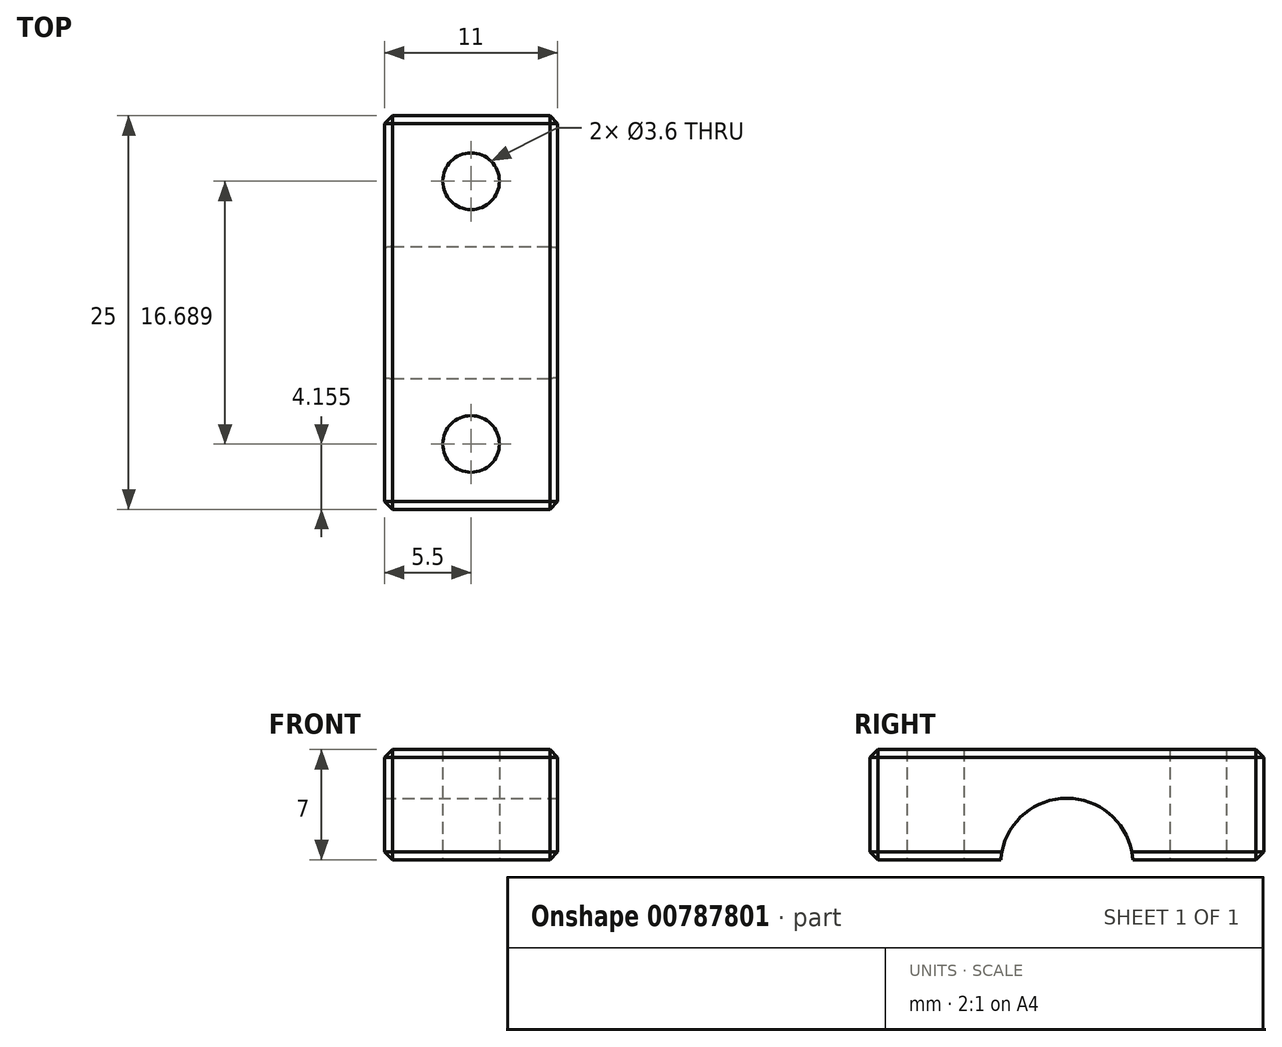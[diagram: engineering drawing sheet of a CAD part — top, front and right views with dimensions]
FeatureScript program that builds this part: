
annotation { "Feature Type Name" : "Feature", "Feature Type Description" : "" }
export const myFeature = defineFeature(function(context is Context, id is Id, definition is map)
    precondition{}
    {
        {
            var Q0;
            Q0=qCreatedBy(makeId("Top.planeOp"),FACE);
            var sketch = newSketch(context, id + "F0", { "sketchPlane" : qUnion([Q0])});
            skLineSegment(sketch, "E0.bottom", {"start": v(5.5, 12.5) * mm, "end": v(-5.5, 12.5) * mm});
            skLineSegment(sketch, "E0.top", {"start": v(5.5, -12.5) * mm, "end": v(-5.5, -12.5) * mm});
            skLineSegment(sketch, "E0.left", {"start": v(5.5, 12.5) * mm, "end": v(5.5, -12.5) * mm});
            skLineSegment(sketch, "E0.right", {"start": v(-5.5, 12.5) * mm, "end": v(-5.5, -12.5) * mm});
            skPoint(sketch, "E0.middle", {"position": v(0, 0) * mm});
            skSolve(sketch);
        }
        {
            var Q0;
            Q0=makeQuery(id+"F0.imprint","IMPRINT",FACE,{"disambiguationData":[TD([[makeQuery(id+"F0.imprint","IMPRINT",EDGE,{"derivedFrom":sQuery(id+"F0.wireOp",EDGE,"E0.bottom")}),1.0]])]});
            extrude(context, id + "F1", {"entities" : qUnion([Q0]), "depth" : 7 * mm, "offsetDistance" : 25 * mm});
        }
        {
            var Q0;
            Q0=makeQuery(id+"F1.opExtrude","SWEPT_FACE",FACE,{"disambiguationData":[OSD([sQuery(id+"F0.wireOp",EDGE,"E0.left")])]});
            var sketch = newSketch(context, id + "F2", { "sketchPlane" : qUnion([Q0])});
            skCircle(sketch, "E1", {"center": v(0, -0.3) * mm, "radius": 4.2 * mm});
            skSolve(sketch);
        }
        {
            var Q0;
            {var subQ0=sQuery(id+"F2.wireOp",EDGE,"E1");var subQ1=makeQuery(id+"F1.opExtrude","CAP_EDGE",EDGE,{"disambiguationData":[OSD([sQuery(id+"F0.wireOp",EDGE,"E0.left")])],"isStart":true});var subQ2=makeQuery(id+"F2.imprint","INTERSECT",VERTEX,{"disambiguationData":[OD(0.0)],"derivedFrom":[subQ1,subQ0]});Q0=makeQuery(id+"F2.imprint","IMPRINT",FACE,{"disambiguationData":[TD([[makeQuery(id+"F2.imprint","IMPRINT",EDGE,{"disambiguationData":[TD([[subQ2,-1.0]])],"derivedFrom":subQ0}),1.0]])]});}
            extrude(context, id + "F3", {"entities" : qUnion([Q0]), "operationType" : NewBodyOperationType.REMOVE, "endBound" : BoundingType.UP_TO_NEXT, "oppositeDirection" : true, "depth" : 25 * mm, "offsetDistance" : 25 * mm});
        }
        {
            var Q0;
            {var subQ0=sQuery(id+"F0.wireOp",EDGE,"E0.bottom");var subQ1=sQuery(id+"F0.wireOp",EDGE,"E0.right");var subQ2=sQuery(id+"F0.wireOp",EDGE,"E0.left");Q0=makeQuery(id+"F3.boolean.opBoolean","SPLIT",FACE,{"disambiguationData":[TD([makeQuery(id+"F1.opExtrude","SWEPT_FACE",FACE,{"disambiguationData":[OSD([subQ0])]})])],"derivedFrom":makeQuery(id+"F1.opExtrude","CAP_FACE",FACE,{"disambiguationData":[OSD([subQ0,sQuery(id+"F0.wireOp",EDGE,"E0.top"),subQ2,subQ1])],"isStart":true})});}
            var sketch = newSketch(context, id + "F4", { "sketchPlane" : qUnion([Q0])});
            skCircle(sketch, "E2", {"center": v(0, -8.34) * mm, "radius": 1.8 * mm});
            skPoint(sketch, "E2.centerSnap0", {"position": v(-5.5, -8.34) * mm});
            skLineSegment(sketch, "E3.0", {"start": v(-5.5, 4.19) * mm, "end": v(-5.5, 12.5) * mm});
            skCircle(sketch, "E4", {"center": v(0, 8.34) * mm, "radius": 1.8 * mm});
            skPoint(sketch, "E4.centerSnap0", {"position": v(-5.5, 8.34) * mm});
            skSolve(sketch);
        }
        {
            var Q0;
            Q0=makeQuery(id+"F4.imprint","IMPRINT",FACE,{"disambiguationData":[TD([[makeQuery(id+"F4.imprint","IMPRINT",EDGE,{"derivedFrom":sQuery(id+"F4.wireOp",EDGE,"E4")}),1.0]])]});
            var Q1;
            Q1=makeQuery(id+"F4.imprint","IMPRINT",FACE,{"disambiguationData":[TD([[makeQuery(id+"F4.imprint","IMPRINT",EDGE,{"derivedFrom":sQuery(id+"F4.wireOp",EDGE,"E2")}),1.0]])]});
            extrude(context, id + "F5", {"entities" : qUnion([Q0, Q1]), "operationType" : NewBodyOperationType.REMOVE, "endBound" : BoundingType.UP_TO_NEXT, "oppositeDirection" : true, "depth" : 25 * mm, "offsetDistance" : 25 * mm});
        }
        {
            var Q0;
            Q0=makeQuery(id+"F3.boolean.opBoolean","COPY",EDGE,{"derivedFrom":makeQuery(id+"F3.opExtrude","CAP_EDGE",EDGE,{"disambiguationData":[OSD([sQuery(id+"F2.wireOp",EDGE,"E1")])],"isStart":true})});
            var Q1;
            {var subQ0=sQuery(id+"F0.wireOp",EDGE,"E0.bottom");var subQ1=sQuery(id+"F0.wireOp",EDGE,"E0.left");Q1=makeQuery(id+"F3.boolean.opBoolean","SPLIT",EDGE,{"disambiguationData":[TD([makeQuery(id+"F1.opExtrude","SWEPT_FACE",FACE,{"disambiguationData":[OSD([subQ0])]})])],"derivedFrom":makeQuery(id+"F1.opExtrude","CAP_EDGE",EDGE,{"disambiguationData":[OSD([subQ1])],"isStart":true})});}
            var Q2;
            Q2=makeQuery(id+"F1.opExtrude","CAP_EDGE",EDGE,{"disambiguationData":[OSD([sQuery(id+"F0.wireOp",EDGE,"E0.bottom")])],"isStart":true});
            var Q3;
            {var subQ0=sQuery(id+"F0.wireOp",EDGE,"E0.bottom");var subQ1=sQuery(id+"F0.wireOp",EDGE,"E0.right");Q3=makeQuery(id+"F3.boolean.opBoolean","SPLIT",EDGE,{"disambiguationData":[TD([makeQuery(id+"F1.opExtrude","SWEPT_FACE",FACE,{"disambiguationData":[OSD([subQ0])]})])],"derivedFrom":makeQuery(id+"F1.opExtrude","CAP_EDGE",EDGE,{"disambiguationData":[OSD([subQ1])],"isStart":true})});}
            var Q4;
            {var subQ0=sQuery(id+"F0.wireOp",EDGE,"E0.left");var subQ1=sQuery(id+"F0.wireOp",EDGE,"E0.top");Q4=makeQuery(id+"F3.boolean.opBoolean","SPLIT",EDGE,{"disambiguationData":[TD([makeQuery(id+"F1.opExtrude","SWEPT_FACE",FACE,{"disambiguationData":[OSD([subQ1])]})])],"derivedFrom":makeQuery(id+"F1.opExtrude","CAP_EDGE",EDGE,{"disambiguationData":[OSD([subQ0])],"isStart":true})});}
            var Q5;
            Q5=makeQuery(id+"F1.opExtrude","CAP_EDGE",EDGE,{"disambiguationData":[OSD([sQuery(id+"F0.wireOp",EDGE,"E0.top")])],"isStart":true});
            var Q6;
            {var subQ0=sQuery(id+"F0.wireOp",EDGE,"E0.right");var subQ1=sQuery(id+"F0.wireOp",EDGE,"E0.top");Q6=makeQuery(id+"F3.boolean.opBoolean","SPLIT",EDGE,{"disambiguationData":[TD([makeQuery(id+"F1.opExtrude","SWEPT_FACE",FACE,{"disambiguationData":[OSD([subQ1])]})])],"derivedFrom":makeQuery(id+"F1.opExtrude","CAP_EDGE",EDGE,{"disambiguationData":[OSD([subQ0])],"isStart":true})});}
            var Q7;
            Q7=makeQuery(id+"F1.opExtrude","SWEPT_EDGE",EDGE,{"disambiguationData":[OSD([sQuery(id+"F0.wireOp",EDGE,"E0.top"),sQuery(id+"F0.wireOp",EDGE,"E0.left")])]});
            var Q8;
            Q8=makeQuery(id+"F1.opExtrude","CAP_EDGE",EDGE,{"disambiguationData":[OSD([sQuery(id+"F0.wireOp",EDGE,"E0.top")])],"isStart":false});
            var Q9;
            Q9=makeQuery(id+"F1.opExtrude","SWEPT_EDGE",EDGE,{"disambiguationData":[OSD([sQuery(id+"F0.wireOp",EDGE,"E0.top"),sQuery(id+"F0.wireOp",EDGE,"E0.right")])]});
            var Q10;
            Q10=makeQuery(id+"F1.opExtrude","CAP_EDGE",EDGE,{"disambiguationData":[OSD([sQuery(id+"F0.wireOp",EDGE,"E0.left")])],"isStart":false});
            var Q11;
            Q11=makeQuery(id+"F1.opExtrude","SWEPT_EDGE",EDGE,{"disambiguationData":[OSD([sQuery(id+"F0.wireOp",EDGE,"E0.bottom"),sQuery(id+"F0.wireOp",EDGE,"E0.left")])]});
            var Q12;
            Q12=makeQuery(id+"F1.opExtrude","CAP_EDGE",EDGE,{"disambiguationData":[OSD([sQuery(id+"F0.wireOp",EDGE,"E0.bottom")])],"isStart":false});
            var Q13;
            Q13=makeQuery(id+"F1.opExtrude","SWEPT_EDGE",EDGE,{"disambiguationData":[OSD([sQuery(id+"F0.wireOp",EDGE,"E0.bottom"),sQuery(id+"F0.wireOp",EDGE,"E0.right")])]});
            var Q14;
            Q14=makeQuery(id+"F1.opExtrude","CAP_EDGE",EDGE,{"disambiguationData":[OSD([sQuery(id+"F0.wireOp",EDGE,"E0.right")])],"isStart":false});
            var Q15;
            {var subQ0=sQuery(id+"F2.wireOp",EDGE,"E1");var subQ1=makeQuery(id+"F1.opExtrude","CAP_EDGE",EDGE,{"disambiguationData":[OSD([sQuery(id+"F0.wireOp",EDGE,"E0.left")])],"isStart":true});Q15=makeQuery(id+"F3.boolean.opBoolean","COPY",EDGE,{"derivedFrom":makeQuery(id+"F3.opExtrude","TWEAK_EDGE",EDGE,{"derivedFrom":[makeQuery(id+"F1.opExtrude","SWEPT_FACE",FACE,{"disambiguationData":[OSD([sQuery(id+"F0.wireOp",EDGE,"E0.right")])]}),makeQuery(id+"F2.imprint","IMPRINT",EDGE,{"disambiguationData":[TD([[makeQuery(id+"F2.imprint","INTERSECT",VERTEX,{"disambiguationData":[OD(0.0)],"derivedFrom":[subQ1,subQ0]}),-1.0]])],"derivedFrom":subQ0})]})});}
            chamfer(context, id + "F6", {"entities" : qUnion([Q0, Q1, Q2, Q3, Q4, Q5, Q6, Q7, Q8, Q9, Q10, Q11, Q12, Q13, Q14, Q15]), "width" : 0.5 * mm, "tangentPropagation" : true});
        }
    });
